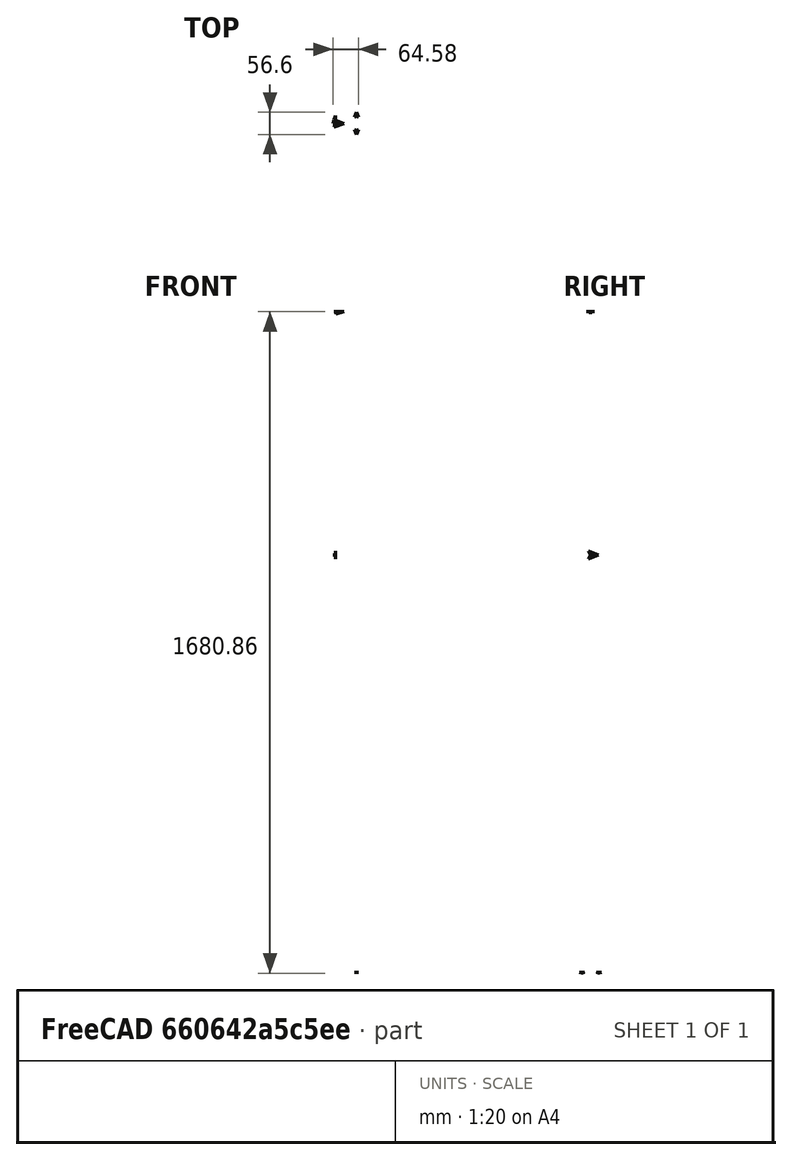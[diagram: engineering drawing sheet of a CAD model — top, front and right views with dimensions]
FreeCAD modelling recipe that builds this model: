
FCSTD DOCUMENT  (FreeCAD 1.1R38827 (Git))
Label: composit_stand3_bar_main
License: All rights reserved
LicenseURL: http://en.wikipedia.org/wiki/All_rights_reserved
objects: Part::FeaturePython×4, Sketcher::SketchObject×2, Spreadsheet::Sheet×1, PartDesign::SubShapeBinder×1
note: 9 computed .brp shape members not serialized (recipe doc carries the construction recipe); baked Part::Feature solids carry a one-line shape summary decoded from their .brp
EXTERNAL_REF file=composit_stand3_bar_bottom_main.FCStd obj=Spreadsheet
EXTERNAL_REF file=../ULZ-P02-14W.FCStd obj=Sketch

FEATURE [Sketcher::SketchObject] Sketch  label="base_Sketch"
  ArcFitTolerance = 0
  FullyConstrained = true
  MakeInternals = false
  expr: .Constraints.length = <<Properties>>.length
  expr: .Constraints.width = <<Properties>>.width
  sketch-geometry (5):
    g0: LineSegment StartX=19 StartY=18.3 StartZ=0 EndX=0 EndY=18.3 EndZ=0
    g1: LineSegment StartX=0 StartY=18.3 StartZ=0 EndX=0 EndY=-18.3 EndZ=0
    g2: LineSegment StartX=0 StartY=-18.3 StartZ=0 EndX=19 EndY=-18.3 EndZ=0
    g3: LineSegment [constr] StartX=19 StartY=-18.3 StartZ=0 EndX=19 EndY=18.3 EndZ=0
    g4: GeomPoint [constr] X=9.5 Y=0 Z=0
  constraints (13):
    c: Coincident(g0,g1)
    c: Coincident(g1,g2)
    c: Coincident(g2,g3)
    c: Coincident(g3,g0)
    c: Horizontal(g0)
    c: Horizontal(g2)
    c: Vertical(g1)
    c: Vertical(g3)
    c: Symmetric(g2,g0,g4)
    c: PointOnObject(g4,g-1)
    c: PointOnObject(g1,g-2)
    c: DistanceX(g1,g0) = 19  'length'
    c: DistanceY(g1,g0) = 36.6  'width'
FEATURE [Spreadsheet::Sheet] Spreadsheet  label="Properties"
  cells = B2(width)==36.6 mm; C2(length)==19 mm; D2(height)==1684 mm; E2(thickness)==2 mm
FEATURE [Part::FeaturePython] Placment  label="bottom_placement"  # WARN: FeaturePython — macro-defined, semantics opaque (R4)
  AttacherType = Attacher::AttachEngine3D
  ExposePlacement = true
  MarkerShape = 1
  MarkerSize = 10
  NumElements = 1
  Placement = pos=(54,18.3,0) rot=(0,0,1;1.5708rad)
  Type = lattice2AttachablePlacement.AttachablePlacement
  isLattice = 1
  expr: .Placement.Base.x = <<composit_stand3_bar_bottom_main>>#<<Properties>>.width / 2 + 4 mm
  expr: .Placement.Base.y = <<Properties>>.width / 2
FEATURE [Part::FeaturePython] Placment001  label="bottom_placement2"  # WARN: FeaturePython — macro-defined, semantics opaque (R4)
  AttacherType = Attacher::AttachEngine3D
  ExposePlacement = true
  MarkerShape = 1
  MarkerSize = 10
  NumElements = 1
  Placement = pos=(54,-18.3,0) rot=(0,0,-1;1.5708rad)
  Type = lattice2AttachablePlacement.AttachablePlacement
  isLattice = 1
  expr: .Placement.Base.x = <<bottom_placement>>.Placement.Base.x
  expr: .Placement.Base.y = -<<bottom_placement>>.Placement.Base.y
FEATURE [Part::FeaturePython] Placment003  label="lamp_placement"  # WARN: FeaturePython — macro-defined, semantics opaque (R4)
  AttacherType = Attacher::AttachEngine3D
  ExposePlacement = true
  MarkerShape = 1
  MarkerSize = 20
  NumElements = 1
  Placement = pos=(0,0,1060) rot=(0.57735,0.57735,0.57735;2.0944rad)
  Type = lattice2AttachablePlacement.AttachablePlacement
  isLattice = 1
  expr: .Placement.Base.z = <<Properties>>.height - 624 mm
FEATURE [Part::FeaturePython] Placment004  label="top_part_placement"  # WARN: FeaturePython — macro-defined, semantics opaque (R4)
  AttacherType = Attacher::AttachEngine3D
  ExposePlacement = true
  MarkerShape = 1
  MarkerSize = 20
  NumElements = 1
  Placement = pos=(2,0,1678) rot=(0,0,1;0rad)
  Type = lattice2AttachablePlacement.AttachablePlacement
  isLattice = 1
  expr: .Placement.Base.x = <<Properties>>.thickness
  expr: .Placement.Base.z = <<Properties>>.height - 6 mm
FEATURE [PartDesign::SubShapeBinder] Binder  label="lamp_holes_import"
  BindCopyOnChange = 0
  BindMode = 0
  ClaimChildren = false
  Fuse = false
  MakeFace = true
  OffsetFill = false
  OffsetIntersection = false
  OffsetJoinType = 0
  OffsetOpenResult = false
  PartialLoad = false
  Relative = true
  Support = -> [<external ../ULZ-P02-14W.FCStd>#Sketch]
  _Version = 2
FEATURE [Sketcher::SketchObject] Sketch001  label="lamp_holes_sketch"
  ArcFitTolerance = 0
  ExternalGeometry = -> [Binder]
  FullyConstrained = true
  MakeInternals = false
  sketch-geometry (12):
    g0: Circle CenterX=-4.15 CenterY=445 CenterZ=0 NormalX=0 NormalY=0 NormalZ=1 AngleXU=0 Radius=1.7
    g1: Circle CenterX=4.15 CenterY=445 CenterZ=0 NormalX=0 NormalY=0 NormalZ=1 AngleXU=0 Radius=1.7
    g2: ArcOfCircle CenterX=4.15 CenterY=-446 CenterZ=0 NormalX=0 NormalY=0 NormalZ=1 AngleXU=0 Radius=1.7 StartAngle=3.14159 EndAngle=6.28319
    g3: ArcOfCircle CenterX=4.15 CenterY=-444 CenterZ=0 NormalX=0 NormalY=0 NormalZ=1 AngleXU=0 Radius=1.7 StartAngle=-2.7e-15 EndAngle=3.14159
    g4: LineSegment StartX=2.45 StartY=-446 StartZ=0 EndX=2.45 EndY=-444 EndZ=0
    g5: LineSegment StartX=5.85 StartY=-446 StartZ=0 EndX=5.85 EndY=-444 EndZ=0
    g6: ArcOfCircle CenterX=-4.15 CenterY=-446 CenterZ=0 NormalX=0 NormalY=0 NormalZ=1 AngleXU=0 Radius=1.7 StartAngle=3.14159 EndAngle=6.28319
    g7: ArcOfCircle CenterX=-4.15 CenterY=-444 CenterZ=0 NormalX=0 NormalY=0 NormalZ=1 AngleXU=0 Radius=1.7 StartAngle=1.11e-14 EndAngle=3.14159
    g8: LineSegment StartX=-5.85 StartY=-446 StartZ=0 EndX=-5.85 EndY=-444 EndZ=0
    g9: LineSegment StartX=-2.45 StartY=-446 StartZ=0 EndX=-2.45 EndY=-444 EndZ=0
    g10: LineSegment [constr] StartX=4.15 StartY=-446 StartZ=0 EndX=4.15 EndY=-445 EndZ=0
    g11: LineSegment [constr] StartX=4.15 StartY=-445 StartZ=0 EndX=4.15 EndY=-444 EndZ=0
  constraints (26):
    c: Coincident(g0,g-3)
    c: Tangent(g2,g4) = 1.5708
    c: Tangent(g2,g5) = -1.5708
    c: Tangent(g3,g4) = 1.5708
    c: Tangent(g3,g5) = -1.5708
    c: Equal(g2,g3)
    c: Vertical(g4)
    c: Tangent(g6,g8) = 1.5708
    c: Tangent(g6,g9) = -1.5708
    c: Tangent(g7,g8) = 1.5708
    c: Tangent(g7,g9) = -1.5708
    c: Equal(g6,g7)
    c: Equal(g7,g3)
    c: Equal(g0,g1)
    c: Diameter(g0) = 3.4
    c: Symmetric(g1,g0,g-2)
    c: Symmetric(g3,g7,g-2)
    c: Symmetric(g6,g2,g-2)
    c: Coincident(g10,g2)
    c: Coincident(g10,g-4)
    c: Vertical(g10)
    c: Coincident(g10,g11)
    c: Coincident(g11,g3)
    c: DistanceY(g10,g10) = 1
    c: DistanceY(g11,g11) = 1
    c: Equal(g7,g0)
